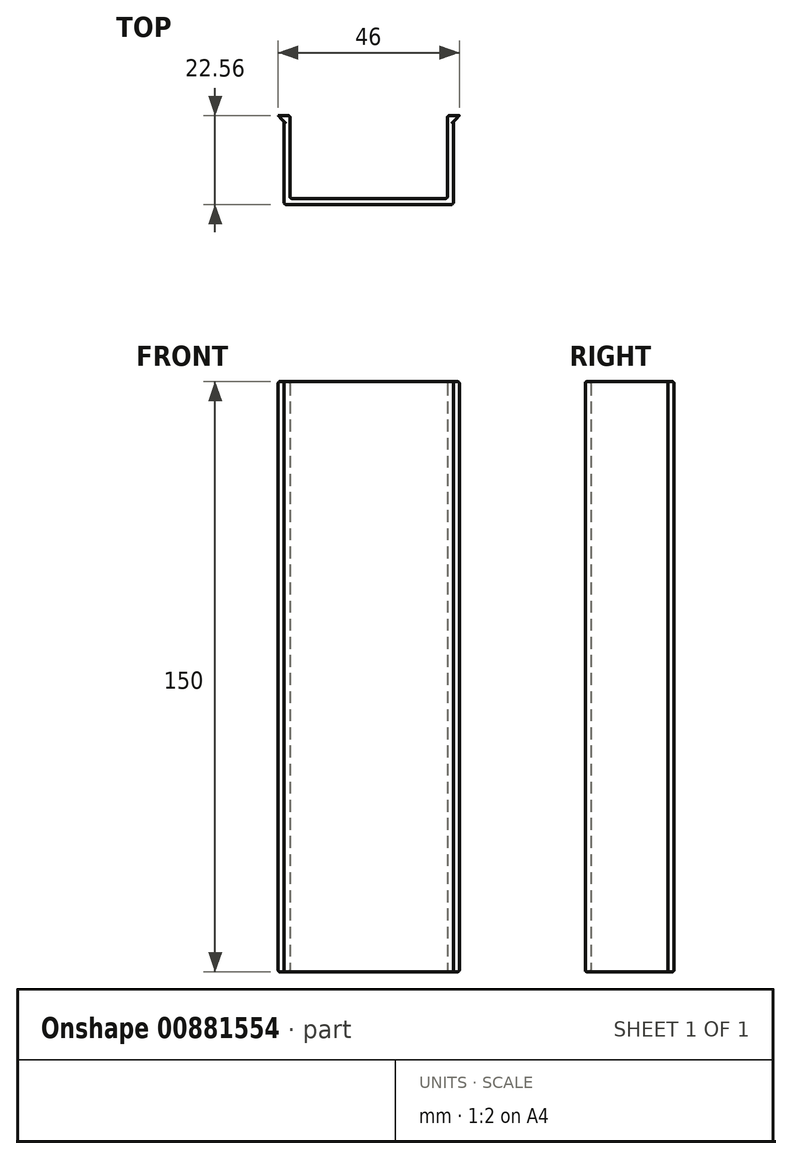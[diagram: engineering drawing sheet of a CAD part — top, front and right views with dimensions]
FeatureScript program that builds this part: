
annotation { "Feature Type Name" : "Feature", "Feature Type Description" : "" }
export const myFeature = defineFeature(function(context is Context, id is Id, definition is map)
    precondition{}
    {
        {
            var Q0;
            Q0=qCreatedBy(makeId("Top.planeOp"),FACE);
            var sketch = newSketch(context, id + "F0", { "sketchPlane" : qUnion([Q0])});
            skLineSegment(sketch, "E0", {"start": v(-41.5, 22.56) * mm, "end": v(-41.5, 1.5) * mm});
            skLineSegment(sketch, "E1", {"start": v(-41.5, 1.5) * mm, "end": v(-1.5, 1.5) * mm});
            skLineSegment(sketch, "E2", {"start": v(-1.5, 1.5) * mm, "end": v(-1.5, 22.56) * mm});
            skLineSegment(sketch, "E3", {"start": v(-1.5, 22.56) * mm, "end": v(1.5, 22.56) * mm});
            skLineSegment(sketch, "E4", {"start": v(1.5, 22.56) * mm, "end": v(0, 21.06) * mm});
            skLineSegment(sketch, "E5", {"start": v(0, 21.06) * mm, "end": v(0, 0) * mm});
            skLineSegment(sketch, "E6", {"start": v(0, 0) * mm, "end": v(-43, 0) * mm});
            skLineSegment(sketch, "E7", {"start": v(-43, 0) * mm, "end": v(-43, 21.06) * mm});
            skLineSegment(sketch, "E8", {"start": v(-43, 21.06) * mm, "end": v(-44.5, 22.56) * mm});
            skLineSegment(sketch, "E9", {"start": v(-44.5, 22.56) * mm, "end": v(-41.5, 22.56) * mm});
            skSolve(sketch);
        }
        {
            var Q0;
            Q0=makeQuery(id+"F0.imprint","IMPRINT",FACE,{"disambiguationData":[TD([[makeQuery(id+"F0.imprint","IMPRINT",EDGE,{"derivedFrom":sQuery(id+"F0.wireOp",EDGE,"E0")}),-1.0]])]});
            extrude(context, id + "F1", {"entities" : qUnion([Q0]), "depth" : 150 * mm, "offsetDistance" : 25 * mm});
        }
        {
            var Q0;
            Q0=makeQuery(id+"F1.opExtrude","SWEPT_EDGE",EDGE,{"disambiguationData":[OSD([sQuery(id+"F0.wireOp",EDGE,"E2"),sQuery(id+"F0.wireOp",EDGE,"E3")])]});
            var Q1;
            Q1=makeQuery(id+"F1.opExtrude","CAP_EDGE",EDGE,{"disambiguationData":[OSD([sQuery(id+"F0.wireOp",EDGE,"E2")])],"isStart":false});
            var Q2;
            Q2=makeQuery(id+"F1.opExtrude","SWEPT_EDGE",EDGE,{"disambiguationData":[OSD([sQuery(id+"F0.wireOp",EDGE,"E1"),sQuery(id+"F0.wireOp",EDGE,"E2")])]});
            var Q3;
            Q3=makeQuery(id+"F1.opExtrude","CAP_EDGE",EDGE,{"disambiguationData":[OSD([sQuery(id+"F0.wireOp",EDGE,"E5")])],"isStart":false});
            var Q4;
            Q4=makeQuery(id+"F1.opExtrude","CAP_EDGE",EDGE,{"disambiguationData":[OSD([sQuery(id+"F0.wireOp",EDGE,"E6")])],"isStart":false});
            var Q5;
            Q5=makeQuery(id+"F1.opExtrude","CAP_EDGE",EDGE,{"disambiguationData":[OSD([sQuery(id+"F0.wireOp",EDGE,"E0")])],"isStart":false});
            var Q6;
            Q6=makeQuery(id+"F1.opExtrude","SWEPT_EDGE",EDGE,{"disambiguationData":[OSD([sQuery(id+"F0.wireOp",EDGE,"E0"),sQuery(id+"F0.wireOp",EDGE,"E9")])]});
            var Q7;
            Q7=makeQuery(id+"F1.opExtrude","CAP_EDGE",EDGE,{"disambiguationData":[OSD([sQuery(id+"F0.wireOp",EDGE,"E1")])],"isStart":true});
            var Q8;
            Q8=makeQuery(id+"F1.opExtrude","CAP_EDGE",EDGE,{"disambiguationData":[OSD([sQuery(id+"F0.wireOp",EDGE,"E1")])],"isStart":false});
            var Q9;
            Q9=makeQuery(id+"F1.opExtrude","SWEPT_EDGE",EDGE,{"disambiguationData":[OSD([sQuery(id+"F0.wireOp",EDGE,"E0"),sQuery(id+"F0.wireOp",EDGE,"E1")])]});
            var Q10;
            Q10=makeQuery(id+"F1.opExtrude","SWEPT_EDGE",EDGE,{"disambiguationData":[OSD([sQuery(id+"F0.wireOp",EDGE,"E5"),sQuery(id+"F0.wireOp",EDGE,"E6")])]});
            var Q11;
            Q11=makeQuery(id+"F1.opExtrude","CAP_EDGE",EDGE,{"disambiguationData":[OSD([sQuery(id+"F0.wireOp",EDGE,"E6")])],"isStart":true});
            var Q12;
            Q12=makeQuery(id+"F1.opExtrude","CAP_EDGE",EDGE,{"disambiguationData":[OSD([sQuery(id+"F0.wireOp",EDGE,"E5")])],"isStart":true});
            var Q13;
            Q13=makeQuery(id+"F1.opExtrude","SWEPT_EDGE",EDGE,{"disambiguationData":[OSD([sQuery(id+"F0.wireOp",EDGE,"E6"),sQuery(id+"F0.wireOp",EDGE,"E7")])]});
            var Q14;
            Q14=makeQuery(id+"F1.opExtrude","CAP_EDGE",EDGE,{"disambiguationData":[OSD([sQuery(id+"F0.wireOp",EDGE,"E7")])],"isStart":false});
            var Q15;
            Q15=makeQuery(id+"F1.opExtrude","CAP_EDGE",EDGE,{"disambiguationData":[OSD([sQuery(id+"F0.wireOp",EDGE,"E7")])],"isStart":true});
            var Q16;
            Q16=makeQuery(id+"F1.opExtrude","CAP_EDGE",EDGE,{"disambiguationData":[OSD([sQuery(id+"F0.wireOp",EDGE,"E0")])],"isStart":true});
            var Q17;
            Q17=makeQuery(id+"F1.opExtrude","CAP_EDGE",EDGE,{"disambiguationData":[OSD([sQuery(id+"F0.wireOp",EDGE,"E2")])],"isStart":true});
            var Q18;
            Q18=makeQuery(id+"F1.opExtrude","CAP_EDGE",EDGE,{"disambiguationData":[OSD([sQuery(id+"F0.wireOp",EDGE,"E9")])],"isStart":false});
            var Q19;
            Q19=makeQuery(id+"F1.opExtrude","CAP_EDGE",EDGE,{"disambiguationData":[OSD([sQuery(id+"F0.wireOp",EDGE,"E3")])],"isStart":false});
            var Q20;
            Q20=makeQuery(id+"F1.opExtrude","CAP_EDGE",EDGE,{"disambiguationData":[OSD([sQuery(id+"F0.wireOp",EDGE,"E3")])],"isStart":true});
            var Q21;
            Q21=makeQuery(id+"F1.opExtrude","CAP_EDGE",EDGE,{"disambiguationData":[OSD([sQuery(id+"F0.wireOp",EDGE,"E9")])],"isStart":true});
            fillet(context, id + "F2", {"entities" : qUnion([Q0, Q1, Q2, Q3, Q4, Q5, Q6, Q7, Q8, Q9, Q10, Q11, Q12, Q13, Q14, Q15, Q16, Q17, Q18, Q19, Q20, Q21]), "radius" : 0.5 * mm, "tangentPropagation" : true, "allowEdgeOverflow" : false});
        }
    });
